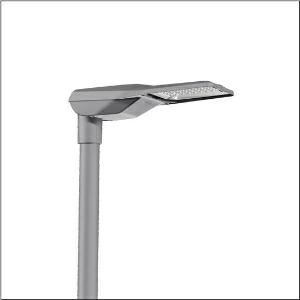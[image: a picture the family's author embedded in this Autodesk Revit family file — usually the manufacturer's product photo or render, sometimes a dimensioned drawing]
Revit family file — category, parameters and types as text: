
# Revit family: streetlight_sl_21_iq_mini___st0_8a_5xe2c21g08hb_0b1a
name_source: partatom
category: Lighting Fixtures
units: mm (PartAtom-declared; Revit-internal decimal feet)

## family parameters
Cut with Voids When Loaded = No
Host = Face
Light Source = No
Part Type = Normal
Room Calculation Point = No
Round Connector Dimension = Use Diameter
Shared = No

## types (1)
- --- (1 x LED, 7830 lm, 70.9 W, 2200K)
    Apparent Load = 71 VA
    CIE Flux Codes = 38 75 97 100 100
    Color Rendering = 70
    Color Temperature = 2200K
    Default Elevation = 1800 mm
    Description = Streetlight SL 21 iQ mini, mast luminaire, primary light control with lens, of PMMA, primary optical cover: cover, of toughened safety glass, transparent, light distribution: ST0.8a, light emission: direct distribution, primary light characteristic: asymmetric, installation type: post-top, side-entry, LED, High Power LED, rated luminous flux: 7.830lm, luminous efficacy: 110lm/W, light colour: 722, colour temperature: 2200K, control: Street-Remote, Auto-Match, Temp-Guard, Lumen-Switch, Night-Set, Smart-Wire, Light-Fading, Desk-Remote (wireless, voltage-free reading and setting of iQ features in the workshop via application-optimized NFC function/RFID function), optimised constant luminous flux control (CLO 2.0), presetting dimming linear, mains connection: 220..240V, AC, 50/60Hz, start of lifetime: 71W, end of service life: 75W, reduction: 31W, luminaire housing, of diecast aluminium, powder-coated, Siteco® metallic grey (DB 702S), corrosivity category C5 mid according to DIN EN ISO 12944, please order mast flange separately, inclination adjustable: 0°, 5°, 10°, 15°, sealing non-destructively replaceable, multi-level sealing system, length: 628mm, width: 235mm, height: 110mm, mast flange for spigot size: 42mm (side-entry): 5XC10008XM4, 60/48mm (side-entry/post-top): 5XC10108XM2, 76/60mm (side-entry/post-top): 5XC10108XM1, protection rating (complete): IP66, insulation class (complete): insulation class II (safety insulation), certification: CE, ENEC, ENEC+, VDE, impact resistance: IK09, permissible operating ambient temperature for outdoor applications: -40..+50°C, standard-compliant lighting for roads and squares, packaging unit: 1 piece

Light Distribution: ST0.8a
    Height = 110 mm
    Lamp = 1 x LED
    Lamp Light Flux = 7830 lm
    Lamp Power = 70.9 W
    Lamp count = 1
    Length = 625 mm
    Luminous efficacy = 110 lm/W
    Manufacturer = Siteco
    ModVariant = No
    Model = 5XE2C21G08HB
    Number of Poles = 1
    OnlyDefault = Yes
    Power Factor = 1
    Product Name = Streetlight SL 21 iQ mini | ST0.8a
    Product group = mast luminaire | pylon top
    ProductGroupID = 6100
    Protection Class = Protection class II
    Protection Degree = IP 66
    RLX_Detail_Level = 1
    RLX_Emergency_Light_Flux = 0 lm
    RLX_Emergency_Type = 0
    RLX_Emergency_Type_DB = No
    RlxData = <blob elided: 92281 chars, md5=c95ecb66>
    Socket = socket
    Standby Power = 0 W
    System Light Flux = 7830 lm
    System Power = 71 W
    Type Comments = factory setting: luminous flux: 100 % | dim-lin: 254 | 711 mA
    Type Image = l_1003519.jpg
    URL = http://relux.com
    VarID = @adj_089849
    Voltage = 0 V
    Weight = 0.00 kg
    Width = 234 mm

## geometry (parser evidence)
native form markers: Blend x4, Sweep x12
no freeform markers — native parametric forms only
